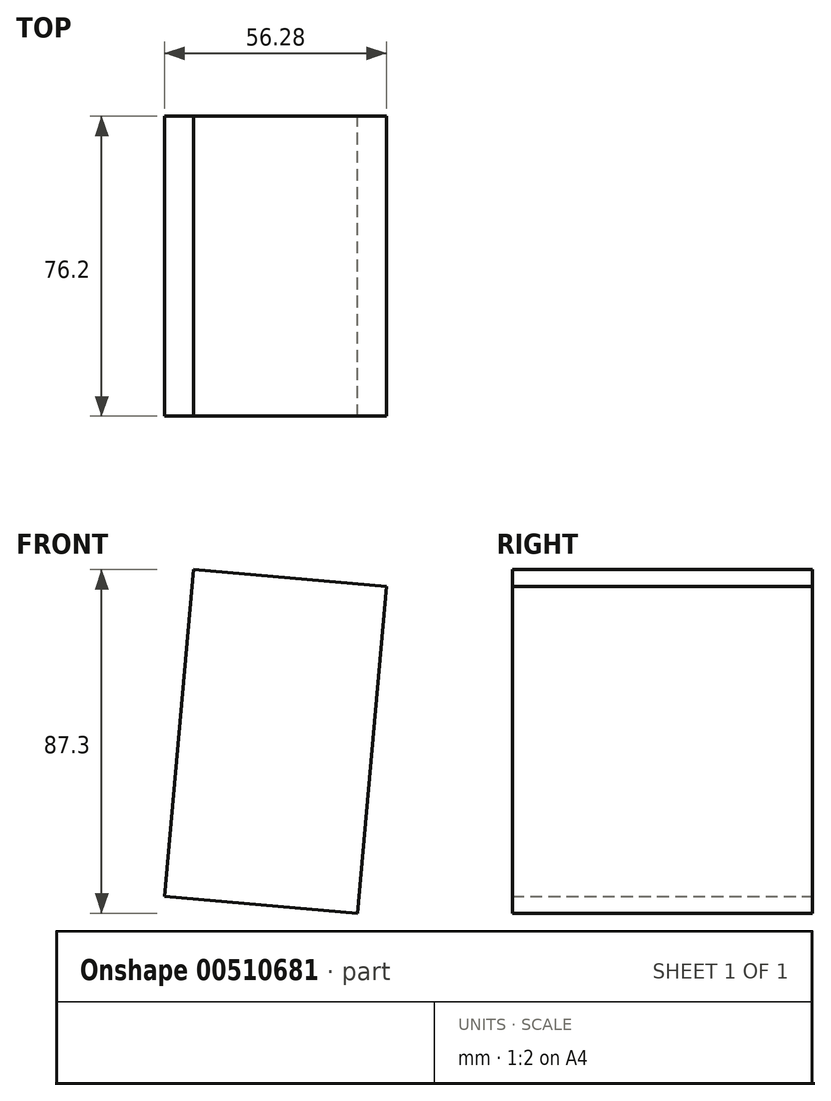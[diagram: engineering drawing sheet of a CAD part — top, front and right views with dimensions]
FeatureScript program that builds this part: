
annotation { "Feature Type Name" : "Feature", "Feature Type Description" : "" }
export const myFeature = defineFeature(function(context is Context, id is Id, definition is map)
    precondition{}
    {
        {
            var Q0;
            Q0=qCreatedBy(makeId("Front.planeOp"),FACE);
            var sketch = newSketch(context, id + "F0", { "sketchPlane" : qUnion([Q0])});
            skLineSegment(sketch, "E0.bottom", {"start": v(-17.34, 41.7) * mm, "end": v(31.68, 37.42) * mm});
            skLineSegment(sketch, "E0.top", {"start": v(-24.6, -41.31) * mm, "end": v(24.42, -45.6) * mm});
            skLineSegment(sketch, "E0.left", {"start": v(-17.34, 41.7) * mm, "end": v(-24.6, -41.31) * mm});
            skLineSegment(sketch, "E0.right", {"start": v(31.68, 37.42) * mm, "end": v(24.42, -45.6) * mm});
            skPoint(sketch, "E0.middle", {"position": v(0, 0) * mm});
            skSolve(sketch);
        }
        {
            var Q0;
            Q0=makeQuery(id+"F0.imprint","IMPRINT",FACE,{"disambiguationData":[TD([[makeQuery(id+"F0.imprint","IMPRINT",EDGE,{"derivedFrom":sQuery(id+"F0.wireOp",EDGE,"E0.bottom")}),-1.0]])]});
            extrude(context, id + "F1", {"entities" : qUnion([Q0]), "depth" : 76.2 * mm, "offsetDistance" : 25.4 * mm});
        }
    });
